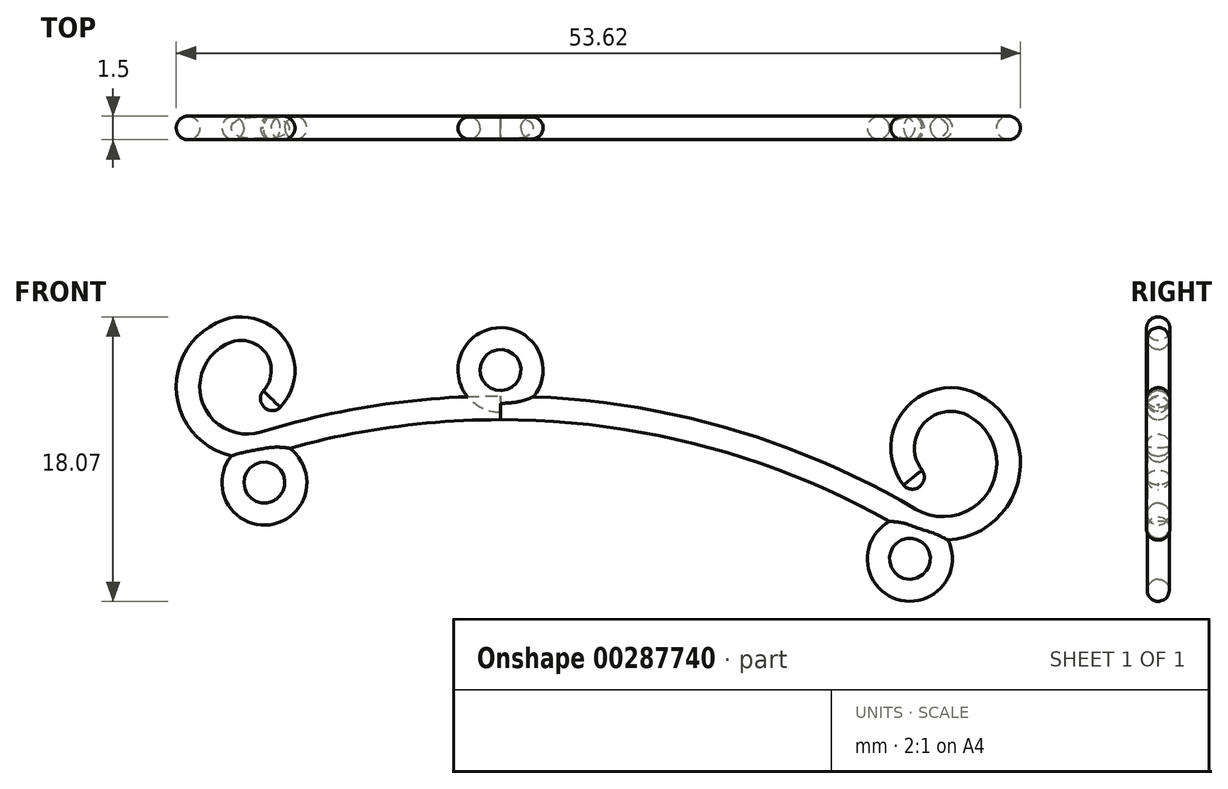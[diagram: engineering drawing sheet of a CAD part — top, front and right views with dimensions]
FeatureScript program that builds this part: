
annotation { "Feature Type Name" : "Feature", "Feature Type Description" : "" }
export const myFeature = defineFeature(function(context is Context, id is Id, definition is map)
    precondition{}
    {
        {
            var Q0;
            Q0=qCreatedBy(makeId("Right.planeOp"),FACE);
            var sketch = newSketch(context, id + "F0", { "sketchPlane" : qUnion([Q0])});
            skCircle(sketch, "E0", {"center": v(0, 2) * mm, "radius": 0.7 * mm});
            skLineSegment(sketch, "E1", {"start": v(0, 0) * mm, "end": v(2.92, 0) * mm, "construction": true});
            skSolve(sketch);
        }
        {
            var Q0;
            Q0=makeQuery(id+"F0.imprint","IMPRINT",FACE,{"disambiguationData":[TD([[makeQuery(id+"F0.imprint","IMPRINT",EDGE,{"derivedFrom":sQuery(id+"F0.wireOp",EDGE,"E0")}),1.0]])]});
            var Q1;
            Q1=sQuery(id+"F0.wireOp",EDGE,"E0");
            var Q2;
            Q2=sQuery(id+"F0.wireOp",EDGE,"E1");
            revolve(context, id + "F1", {"entities" : qUnion([Q0]), "surfaceEntities" : qUnion([Q1]), "axis" : qUnion([Q2]), "revolveType" : RevolveType.FULL});
        }
        {
            var Q0;
            Q0=qCreatedBy(makeId("Right.planeOp"),FACE);
            var sketch = newSketch(context, id + "F2", { "sketchPlane" : qUnion([Q0])});
            skCircle(sketch, "E2", {"center": v(0, -2.4) * mm, "radius": 0.75 * mm});
            skSolve(sketch);
        }
        {
            var Q0;
            Q0=qCreatedBy(makeId("Front.planeOp"),FACE);
            var sketch = newSketch(context, id + "F3", { "sketchPlane" : qUnion([Q0])});
            skArc(sketch, "E3", {"start": v(26, -9.49) * mm, "mid": v(13.47, -4.2) * mm, "end": v(0, -2.4) * mm});
            skArc(sketch, "E4", {"start": v(-15, -4.64) * mm, "mid": v(-19.66, -2.23) * mm, "end": v(-17.34, 2.48) * mm});
            skArc(sketch, "E5", {"start": v(-17.34, 2.48) * mm, "mid": v(-14.07, 1.12) * mm, "end": v(-15.07, -2.28) * mm});
            skArc(sketch, "E6", {"start": v(26, -9.49) * mm, "mid": v(31.75, -7.91) * mm, "end": v(30.02, -2.2) * mm});
            skArc(sketch, "E7", {"start": v(30.02, -2.2) * mm, "mid": v(26.03, -3.26) * mm, "end": v(26.68, -7.33) * mm});
            skArc(sketch, "E8", {"start": v(0, -2.4) * mm, "mid": v(-7.58, -2.96) * mm, "end": v(-15, -4.64) * mm});
            skSolve(sketch);
        }
        {
            var Q0;
            Q0=makeQuery(id+"F2.imprint","IMPRINT",FACE,{"disambiguationData":[TD([[makeQuery(id+"F2.imprint","IMPRINT",EDGE,{"derivedFrom":sQuery(id+"F2.wireOp",EDGE,"E2")}),1.0]])]});
            var Q1;
            Q1=sQuery(id+"F3.wireOp",EDGE,"E3");
            var Q2;
            Q2=sQuery(id+"F3.wireOp",EDGE,"E6");
            var Q3;
            Q3=sQuery(id+"F3.wireOp",EDGE,"E7");
            sweep(context, id + "F4", {"operationType" : NewBodyOperationType.ADD, "profiles" : qUnion([Q0]), "path" : qUnion([Q1, Q2, Q3])});
        }
        {
            var Q0;
            Q0=makeQuery(id+"F2.imprint","IMPRINT",FACE,{"disambiguationData":[TD([[makeQuery(id+"F2.imprint","IMPRINT",EDGE,{"derivedFrom":sQuery(id+"F2.wireOp",EDGE,"E2")}),1.0]])]});
            var Q1;
            Q1=sQuery(id+"F2.wireOp",EDGE,"E2");
            var Q2;
            Q2=sQuery(id+"F3.wireOp",EDGE,"E8");
            var Q3;
            Q3=sQuery(id+"F3.wireOp",EDGE,"E4");
            var Q4;
            Q4=sQuery(id+"F3.wireOp",EDGE,"E5");
            sweep(context, id + "F5", {"profiles" : qUnion([Q0]), "surfaceProfiles" : qUnion([Q1]), "path" : qUnion([Q2, Q3, Q4])});
        }
        {
            var Q0;
            Q0=qCreatedBy(makeId("Front.planeOp"),FACE);
            var sketch = newSketch(context, id + "F6", { "sketchPlane" : qUnion([Q0])});
            skPoint(sketch, "E9", {"position": v(26, -11.99) * mm});
            skPoint(sketch, "E10", {"position": v(-15, -7.14) * mm});
            skLineSegment(sketch, "E11", {"start": v(0, 0) * mm, "end": v(15.34, 0) * mm});
            skLineSegment(sketch, "E12", {"start": v(0, 0) * mm, "end": v(0, -9.1) * mm});
            skSolve(sketch);
        }
        {
            var Q0;
            Q0=qCreatedBy(makeId("Top.planeOp"),FACE);
            var Q1;
            Q1=sQuery(id+"F6.wireOp",VERTEX,"E9");
            cPlane(context, id + "F7", {"entities" : qUnion([Q0, Q1]), "cplaneType" : CPlaneType.PLANE_POINT, "offset" : 25 * mm, "width" : 150 * mm, "height" : 150 * mm});
        }
        {
            var Q0;
            Q0=qCreatedBy(makeId("Top.planeOp"),FACE);
            var Q1;
            Q1=sQuery(id+"F6.wireOp",VERTEX,"E10");
            cPlane(context, id + "F8", {"entities" : qUnion([Q0, Q1]), "cplaneType" : CPlaneType.PLANE_POINT, "offset" : 25 * mm, "width" : 150 * mm, "height" : 150 * mm});
        }
        {
            var Q0;
            Q0=qCreatedBy(id+"F7.planeOp",FACE);
            var sketch = newSketch(context, id + "F9", { "sketchPlane" : qUnion([Q0])});
            skLineSegment(sketch, "E13", {"start": v(26, 0) * mm, "end": v(26, -3.23) * mm, "construction": true});
            skCircle(sketch, "E14", {"center": v(28, 0) * mm, "radius": 0.7 * mm});
            skSolve(sketch);
        }
        {
            var Q0;
            Q0=makeQuery(id+"F9.imprint","IMPRINT",FACE,{"disambiguationData":[TD([[makeQuery(id+"F9.imprint","IMPRINT",EDGE,{"derivedFrom":sQuery(id+"F9.wireOp",EDGE,"E14")}),1.0]])]});
            var Q1;
            Q1=sQuery(id+"F9.wireOp",EDGE,"E13");
            revolve(context, id + "F10", {"operationType" : NewBodyOperationType.ADD, "entities" : qUnion([Q0]), "axis" : qUnion([Q1]), "revolveType" : RevolveType.FULL});
        }
        {
            var Q0;
            Q0=qCreatedBy(id+"F8.planeOp",FACE);
            var sketch = newSketch(context, id + "F11", { "sketchPlane" : qUnion([Q0])});
            skLineSegment(sketch, "E15", {"start": v(-15, 0) * mm, "end": v(-15, -1.79) * mm, "construction": true});
            skCircle(sketch, "E16", {"center": v(-17, 0) * mm, "radius": 0.7 * mm});
            skSolve(sketch);
        }
        {
            var Q0;
            Q0 = qSketchRegion(id + "F11", true);
            var Q1;
            Q1=sQuery(id+"F11.wireOp",EDGE,"E15");
            revolve(context, id + "F12", {"operationType" : NewBodyOperationType.ADD, "entities" : qUnion([Q0]), "axis" : qUnion([Q1]), "revolveType" : RevolveType.FULL});
        }
        {
            var Q0;
            Q0=makeQuery(id+"F5.opSweep","CAP_EDGE",EDGE,{"disambiguationData":[OSD([sQuery(id+"F2.wireOp",EDGE,"E2"),sQuery(id+"F3.wireOp",VERTEX,"E5.end")])],"isStart":false});
            var Q1;
            Q1=makeQuery(id+"F4.opSweep","CAP_EDGE",EDGE,{"disambiguationData":[OSD([sQuery(id+"F2.wireOp",EDGE,"E2"),sQuery(id+"F3.wireOp",VERTEX,"E7.end")])],"isStart":false});
            fillet(context, id + "F13", {"entities" : qUnion([Q0, Q1]), "radius" : 0.7 * mm, "tangentPropagation" : true, "allowEdgeOverflow" : false});
        }
    });
